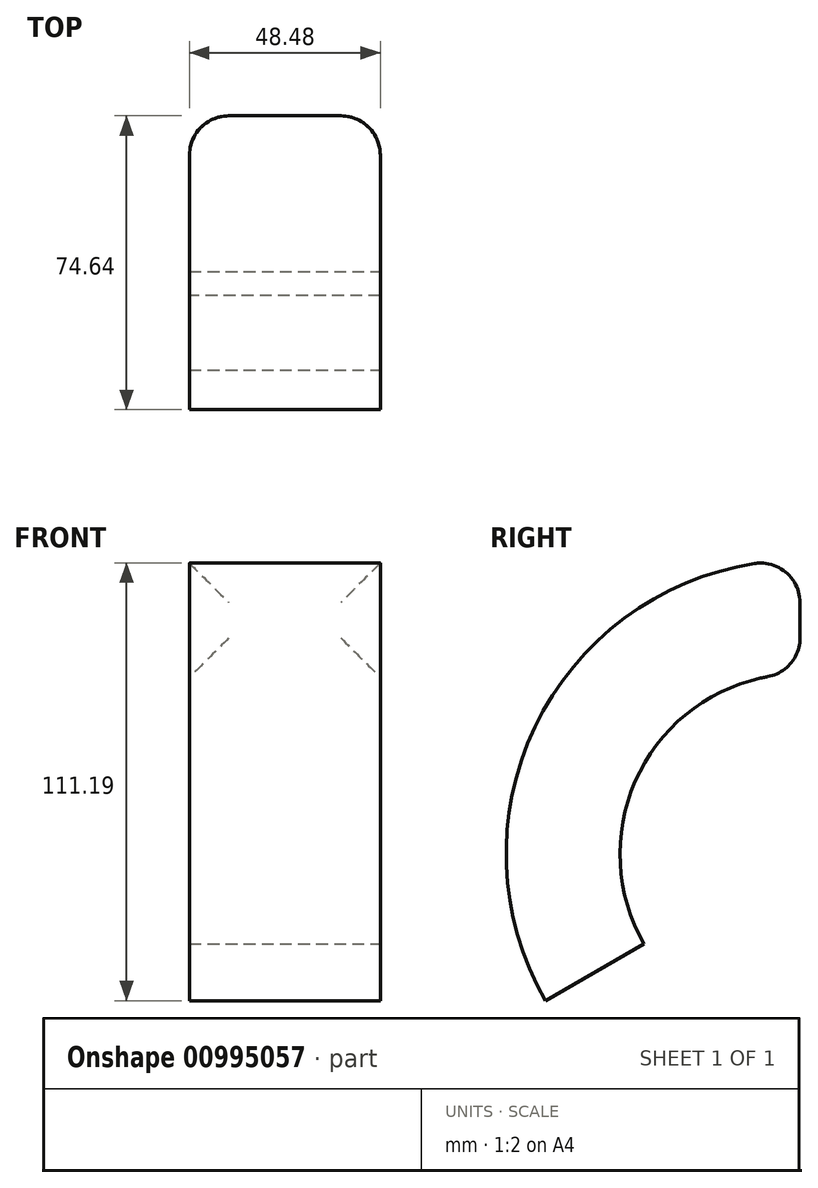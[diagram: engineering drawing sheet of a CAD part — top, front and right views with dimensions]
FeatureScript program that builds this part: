
annotation { "Feature Type Name" : "Feature", "Feature Type Description" : "" }
export const myFeature = defineFeature(function(context is Context, id is Id, definition is map)
    precondition{}
    {
        {
            var Q0;
            Q0=qCreatedBy(makeId("Front.planeOp"),FACE);
            var sketch = newSketch(context, id + "F0", { "sketchPlane" : qUnion([Q0])});
            skLineSegment(sketch, "E0.bottom", {"start": v(-24.24, 14.46) * mm, "end": v(24.24, 14.46) * mm});
            skLineSegment(sketch, "E0.top", {"start": v(-24.24, -14.46) * mm, "end": v(24.24, -14.46) * mm});
            skLineSegment(sketch, "E0.left", {"start": v(-24.24, 14.46) * mm, "end": v(-24.24, -14.46) * mm});
            skLineSegment(sketch, "E0.right", {"start": v(24.24, 14.46) * mm, "end": v(24.24, -14.46) * mm});
            skLineSegment(sketch, "E1", {"start": v(24.24, 14.46) * mm, "end": v(-24.24, -14.46) * mm, "construction": true});
            skLineSegment(sketch, "E2", {"start": v(-24.24, 14.46) * mm, "end": v(24.24, -14.46) * mm, "construction": true});
            skPoint(sketch, "E3", {"position": v(0, 0) * mm});
            skLineSegment(sketch, "E4", {"start": v(-26.35, -60.19) * mm, "end": v(19.9, -60.19) * mm, "construction": true});
            skSolve(sketch);
        }
        {
            var Q0;
            Q0 = qSketchRegion(id + "F0", true);
            var Q1;
            Q1=sQuery(id+"F0.wireOp",EDGE,"E4");
            revolve(context, id + "F1", {"surfaceOperationType" : NewSurfaceOperationType.NEW, "entities" : qUnion([Q0]), "axis" : qUnion([Q1]), "revolveType" : RevolveType.ONE_DIRECTION, "angle" : 120 * degree});
        }
        {
            var Q0;
            Q0=makeQuery(id+"F1.opRevolve","CAP_FACE",FACE,{"disambiguationData":[OSD([sQuery(id+"F0.wireOp",EDGE,"E0.bottom"),sQuery(id+"F0.wireOp",EDGE,"E0.top"),sQuery(id+"F0.wireOp",EDGE,"E0.left"),sQuery(id+"F0.wireOp",EDGE,"E0.right")])],"isStart":true});
            fillet(context, id + "F2", {"entities" : qUnion([Q0]), "radius" : 10 * mm, "tangentPropagation" : true, "allowEdgeOverflow" : false});
        }
    });
